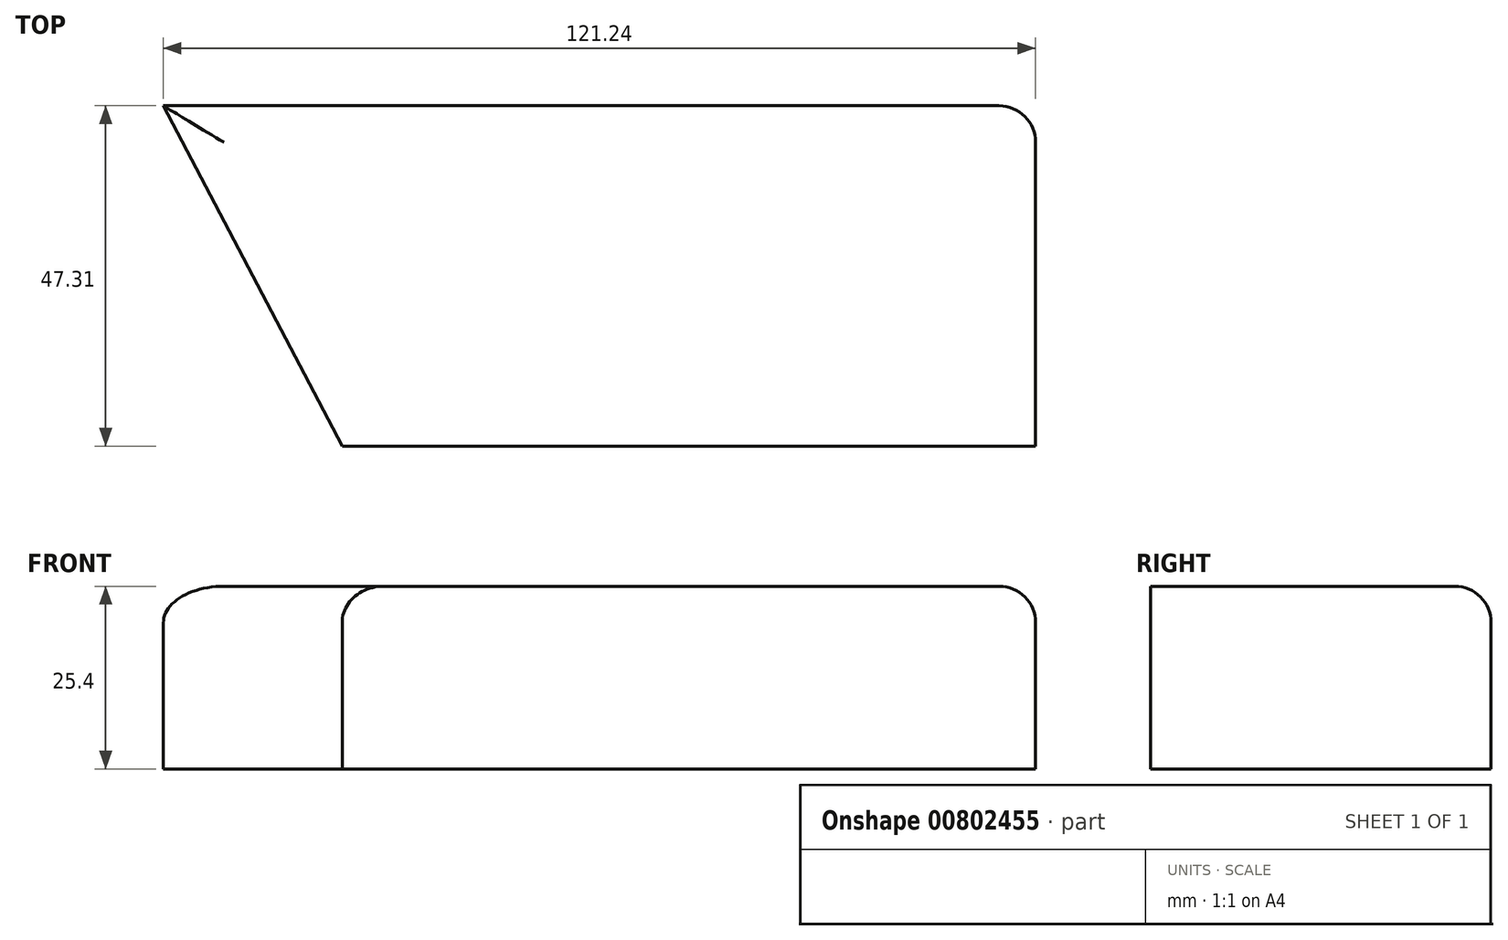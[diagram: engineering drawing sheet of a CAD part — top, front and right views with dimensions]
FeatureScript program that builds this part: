
annotation { "Feature Type Name" : "Feature", "Feature Type Description" : "" }
export const myFeature = defineFeature(function(context is Context, id is Id, definition is map)
    precondition{}
    {
        {
            var Q0;
            Q0=qCreatedBy(makeId("Top.planeOp"),FACE);
            var sketch = newSketch(context, id + "F0", { "sketchPlane" : qUnion([Q0])});
            skLineSegment(sketch, "E0", {"start": v(0, 0) * mm, "end": v(96.38, 0) * mm});
            skLineSegment(sketch, "E1", {"start": v(96.38, 0) * mm, "end": v(96.38, 47.31) * mm});
            skLineSegment(sketch, "E2", {"start": v(96.38, 47.31) * mm, "end": v(-24.86, 47.31) * mm});
            skLineSegment(sketch, "E3", {"start": v(-24.86, 47.31) * mm, "end": v(0, 0) * mm});
            skSolve(sketch);
        }
        {
            var Q0;
            Q0 = qSketchRegion(id + "F0", true);
            extrude(context, id + "F1", {"entities" : qUnion([Q0]), "depth" : 25.4 * mm, "offsetDistance" : 25.4 * mm});
        }
        {
            var Q0;
            Q0=makeQuery(id+"F1.opExtrude","CAP_EDGE",EDGE,{"disambiguationData":[OSD([sQuery(id+"F0.wireOp",EDGE,"E3")])],"isStart":false});
            var Q1;
            Q1=makeQuery(id+"F1.opExtrude","CAP_EDGE",EDGE,{"disambiguationData":[OSD([sQuery(id+"F0.wireOp",EDGE,"E2")])],"isStart":false});
            var Q2;
            Q2=makeQuery(id+"F1.opExtrude","CAP_EDGE",EDGE,{"disambiguationData":[OSD([sQuery(id+"F0.wireOp",EDGE,"E1")])],"isStart":false});
            var Q3;
            Q3=makeQuery(id+"F1.opExtrude","SWEPT_EDGE",EDGE,{"disambiguationData":[OSD([sQuery(id+"F0.wireOp",EDGE,"E1"),sQuery(id+"F0.wireOp",EDGE,"E2")])]});
            fillet(context, id + "F2", {"entities" : qUnion([Q0, Q1, Q2, Q3]), "radius" : 5.08 * mm, "tangentPropagation" : true, "allowEdgeOverflow" : false});
        }
    });
